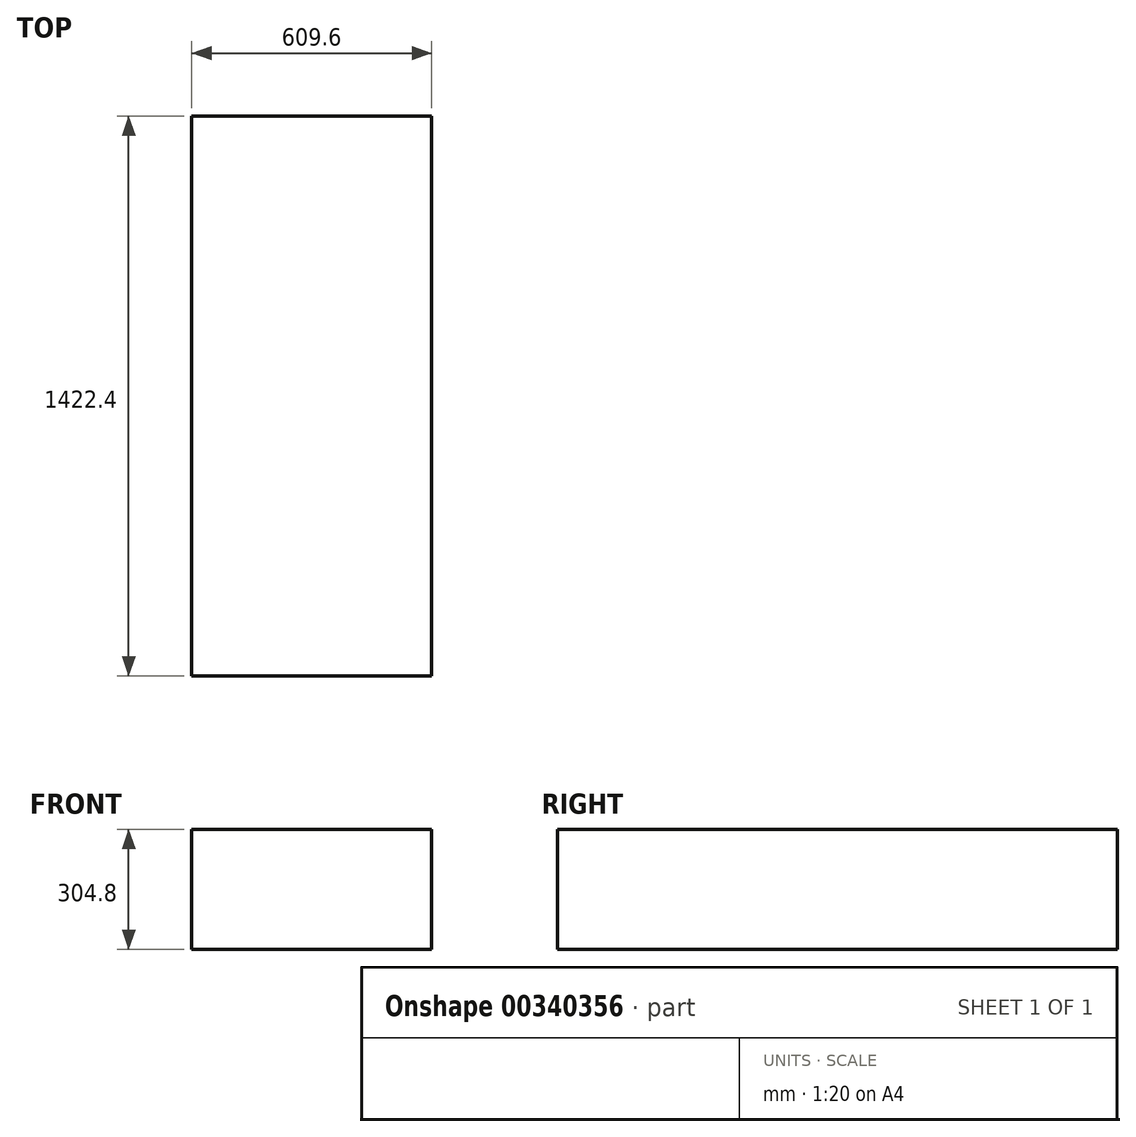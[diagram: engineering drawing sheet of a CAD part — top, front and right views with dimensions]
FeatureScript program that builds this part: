
annotation { "Feature Type Name" : "Feature", "Feature Type Description" : "" }
export const myFeature = defineFeature(function(context is Context, id is Id, definition is map)
    precondition{}
    {
        {
            var Q0;
            Q0=qCreatedBy(makeId("Front.planeOp"),FACE);
            var sketch = newSketch(context, id + "F0", { "sketchPlane" : qUnion([Q0])});
            skLineSegment(sketch, "E0.bottom", {"start": v(0, 0) * mm, "end": v(-609.6, 0) * mm});
            skLineSegment(sketch, "E0.top", {"start": v(0, 304.8) * mm, "end": v(-609.6, 304.8) * mm});
            skLineSegment(sketch, "E0.left", {"start": v(0, 0) * mm, "end": v(0, 304.8) * mm});
            skLineSegment(sketch, "E0.right", {"start": v(-609.6, 0) * mm, "end": v(-609.6, 304.8) * mm});
            skSolve(sketch);
        }
        {
            var Q0;
            Q0=makeQuery(id+"F0.imprint","IMPRINT",FACE,{"disambiguationData":[TD([[makeQuery(id+"F0.imprint","IMPRINT",EDGE,{"derivedFrom":sQuery(id+"F0.wireOp",EDGE,"E0.bottom")}),-1.0]])]});
            extrude(context, id + "F1", {"entities" : qUnion([Q0]), "depth" : 1422.4 * mm});
        }
    });
